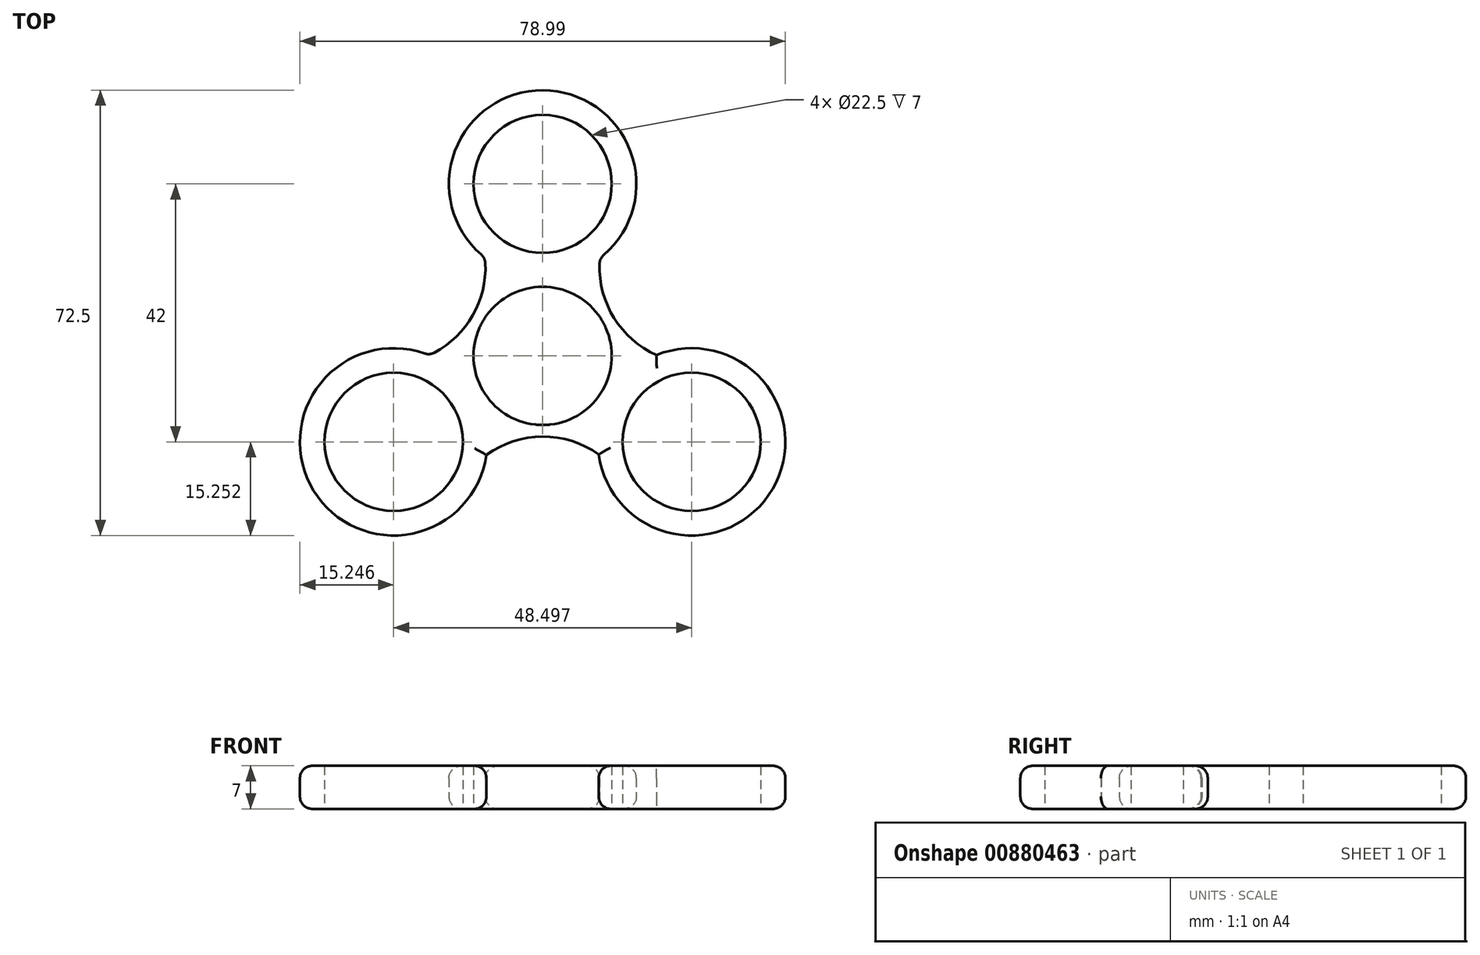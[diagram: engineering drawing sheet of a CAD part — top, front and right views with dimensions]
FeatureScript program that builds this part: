
annotation { "Feature Type Name" : "Feature", "Feature Type Description" : "" }
export const myFeature = defineFeature(function(context is Context, id is Id, definition is map)
    precondition{}
    {
        {
            var Q0;
            Q0=qCreatedBy(makeId("Top.planeOp"),FACE);
            var sketch = newSketch(context, id + "F0", { "sketchPlane" : qUnion([Q0])});
            skCircle(sketch, "E0", {"center": v(-3.62, 1.57) * mm, "radius": 11.25 * mm});
            skCircle(sketch, "E1", {"center": v(-3.62, 29.57) * mm, "radius": 11.25 * mm});
            skCircle(sketch, "E2.1.0", {"center": v(-27.86, -12.43) * mm, "radius": 11.25 * mm});
            skCircle(sketch, "E3.0", {"center": v(-3.62, 29.57) * mm, "radius": 15.25 * mm});
            skCircle(sketch, "E4.0", {"center": v(20.63, -12.43) * mm, "radius": 11.25 * mm});
            skCircle(sketch, "E5.0", {"center": v(-27.86, -12.43) * mm, "radius": 15.25 * mm});
            skCircle(sketch, "E6.0", {"center": v(20.63, -12.43) * mm, "radius": 15.25 * mm});
            skArc(sketch, "E7", {"start": v(-22.08, 1.68) * mm, "mid": v(-14.98, 8.16) * mm, "end": v(-13.01, 17.56) * mm});
            skArc(sketch, "E8.1.0", {"start": v(5.52, -14.47) * mm, "mid": v(-3.64, -11.56) * mm, "end": v(-12.76, -14.56) * mm});
            skArc(sketch, "E8.2.0", {"start": v(5.71, 17.5) * mm, "mid": v(7.77, 8.12) * mm, "end": v(14.93, 1.72) * mm});
            skSolve(sketch);
        }
        {
            var Q0;
            Q0 = qSketchRegion(id + "F0", true);
            extrude(context, id + "F1", {"entities" : qUnion([Q0]), "depth" : 7 * mm, "offsetDistance" : 25 * mm});
        }
        {
            var Q0;
            Q0=makeQuery(id+"F1.opExtrude","SWEPT_FACE",FACE,{"disambiguationData":[OSD([sQuery(id+"F0.wireOp",EDGE,"E3.0")])]});
            var Q1;
            Q1=makeQuery(id+"F1.opExtrude","SWEPT_FACE",FACE,{"disambiguationData":[OSD([sQuery(id+"F0.wireOp",EDGE,"E7")])]});
            var Q2;
            Q2=makeQuery(id+"F1.opExtrude","CAP_EDGE",EDGE,{"disambiguationData":[OSD([sQuery(id+"F0.wireOp",EDGE,"E8.2.0")])],"isStart":false});
            var Q3;
            Q3=makeQuery(id+"F1.opExtrude","CAP_EDGE",EDGE,{"disambiguationData":[OSD([sQuery(id+"F0.wireOp",EDGE,"E6.0")])],"isStart":false});
            var Q4;
            Q4=makeQuery(id+"F1.opExtrude","CAP_EDGE",EDGE,{"disambiguationData":[OSD([sQuery(id+"F0.wireOp",EDGE,"E8.1.0")])],"isStart":false});
            var Q5;
            Q5=makeQuery(id+"F1.opExtrude","CAP_EDGE",EDGE,{"disambiguationData":[OSD([sQuery(id+"F0.wireOp",EDGE,"E5.0")])],"isStart":false});
            var Q6;
            Q6=makeQuery(id+"F1.opExtrude","CAP_EDGE",EDGE,{"disambiguationData":[OSD([sQuery(id+"F0.wireOp",EDGE,"E8.2.0")])],"isStart":true});
            var Q7;
            Q7=makeQuery(id+"F1.opExtrude","CAP_EDGE",EDGE,{"disambiguationData":[OSD([sQuery(id+"F0.wireOp",EDGE,"E5.0")])],"isStart":true});
            var Q8;
            Q8=makeQuery(id+"F1.opExtrude","CAP_EDGE",EDGE,{"disambiguationData":[OSD([sQuery(id+"F0.wireOp",EDGE,"E8.1.0")])],"isStart":true});
            var Q9;
            Q9=makeQuery(id+"F1.opExtrude","CAP_EDGE",EDGE,{"disambiguationData":[OSD([sQuery(id+"F0.wireOp",EDGE,"E6.0")])],"isStart":true});
            fillet(context, id + "F2", {"entities" : qUnion([Q0, Q1, Q2, Q3, Q4, Q5, Q6, Q7, Q8, Q9]), "radius" : 2 * mm, "tangentPropagation" : true, "allowEdgeOverflow" : false});
        }
    });
